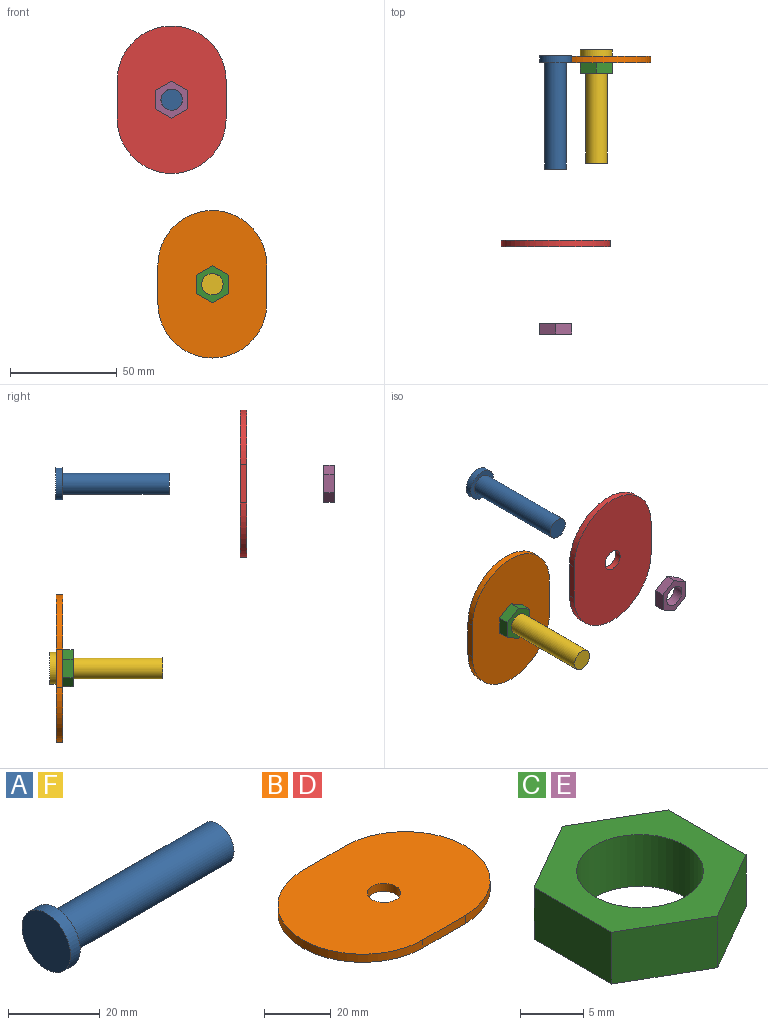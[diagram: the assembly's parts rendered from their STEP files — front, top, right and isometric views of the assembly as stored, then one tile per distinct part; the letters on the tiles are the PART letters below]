
ASSEMBLY  parts=6 mates=6
PART A: 5 faces, bbox 53x15x15 mm
  f0: cylinder r=7.5mm len=15mm, axis (-1,0,0), area 141.4mm2, adj f1,f2
  f1: plane 15x15mm, normal (1,0,0), area 98.2mm2, adj f0,f3
  f2: plane 15x15mm, normal (-1,0,0), area 176.7mm2, adj f0
  f3: cylinder r=5mm len=50mm, axis (-1,0,0), area 1570.8mm2, adj f1,f4
  f4: plane 10x10mm, normal (1,0,0), area 78.5mm2, adj f3
PART B: 7 faces, bbox 69x51x3 mm
  f0: plane 18x3mm, normal (0,1,0), area 54mm2, adj f1,f3,f4,f5
  f1: cylinder r=25.5mm len=51mm, axis (0,0,-1), area 240.3mm2, adj f0,f2,f4,f5
  f2: plane 18x3mm, normal (0,-1,0), area 54mm2, adj f1,f3,f4,f5
  f3: cylinder r=25.5mm len=51mm, axis (0,0,-1), area 240.3mm2, adj f0,f2,f4,f5
  f4: plane 69x51mm, normal (0,0,1), area 2882.3mm2, adj f0,f1,f2,f3,f6
  f5: plane 69x51mm, normal (0,0,-1), area 2882.3mm2, adj f0,f1,f2,f3,f6
  f6: cylinder r=5mm len=10mm, axis (0,0,1), area 94.2mm2, adj f4,f5
PART C: 9 faces, bbox 15x17.3x5 mm
  f0: plane 7.5x5mm, normal (0.5,-0.87,0), area 43.3mm2, adj f1,f5,f6,f7
  f1: plane 8.66x5mm, normal (1,0,0), area 43.3mm2, adj f0,f2,f6,f7
  f2: plane 7.5x5mm, normal (0.5,0.87,0), area 43.3mm2, adj f1,f3,f6,f7
  f3: plane 7.5x5mm, normal (-0.5,0.87,0), area 43.3mm2, adj f2,f4,f6,f7
  f4: plane 8.66x5mm, normal (-1,0,0), area 43.3mm2, adj f3,f5,f6,f7
  f5: plane 7.5x5mm, normal (-0.5,-0.87,0), area 43.3mm2, adj f0,f4,f6,f7
  f6: plane 17.32x15mm, normal (0,0,1), area 116.3mm2, adj f0,f1,f2,f3,f4,f5,f8
  f7: plane 17.32x15mm, normal (0,0,-1), area 116.3mm2, adj f0,f1,f2,f3,f4,f5,f8
  f8: cylinder r=5mm len=10mm, axis (0,0,1), area 157.1mm2, adj f6,f7
PART D: same geometry as B
PART E: same geometry as C
PART F: same geometry as A
PLACE A rot(axis=(0,0,-1),90deg) t=(-52.81,78.44,68.6)mm
PLACE B rot(axis=(-0.58,-0.58,-0.58),120deg) t=(-53.94,75.39,62.54)mm
PLACE C rot(axis=(-1,0,0),90deg) t=(22.93,70.39,8.39)mm
PLACE D rot(axis=(-0.58,-0.58,-0.58),120deg) t=(-72.99,-10.91,148.93)mm fixed
PLACE E rot(axis=(-1,0,0),90deg) t=(3.87,-51.83,94.79)mm
PLACE F rot(axis=(0,0,-1),90deg) t=(-33.75,81.39,-17.8)mm
MATE fastened C.f8 <-> B.f6  axis (0,1,0) through (-13.08,75.39,-7.79)mm
MATE slider E.f8 <-> D.f6  axis (0,-1,0) through (-32.14,-51.83,78.61)mm
MATE slider F.f0 <-> B.f6  axis (0,1,0) through (-13.08,53.39,-7.79)mm
MATE fastened F.f0 <-> B.f6  axis (0,-1,0) through (-13.08,78.39,-7.79)mm
MATE slider A.f0 <-> D.f6  axis (0,1,0) through (-32.14,50.44,78.61)mm
MATE slider C.f8 <-> B.f6  axis (0,-1,0) through (-13.08,70.39,-7.79)mm
